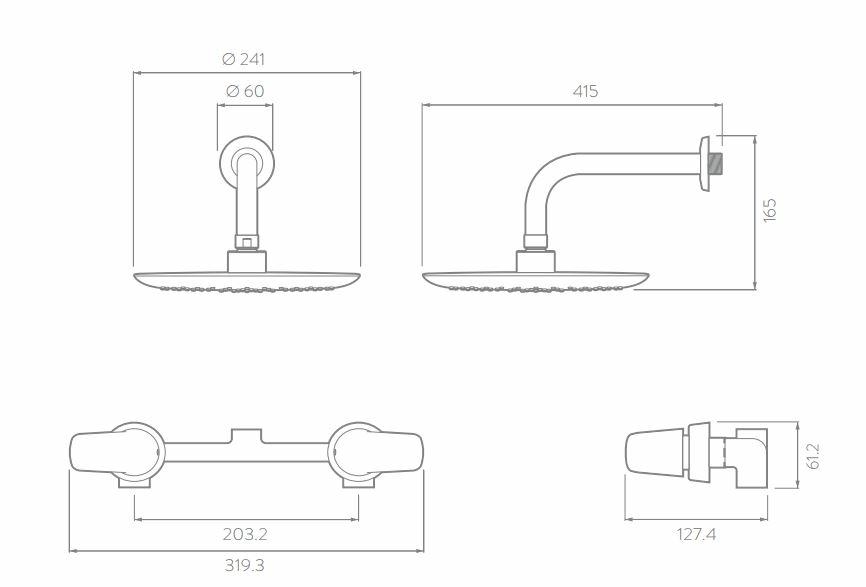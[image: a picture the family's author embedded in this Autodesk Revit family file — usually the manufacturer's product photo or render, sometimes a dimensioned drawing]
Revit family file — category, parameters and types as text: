
# Revit family: LQ4045551  LQ4055551_Ducha 8 pulgadas SD Liquid
name_source: partatom
category: Plumbing Fixtures
units: mm (PartAtom-declared; Revit-internal decimal feet)

## family parameters
Always vertical = Yes
Cut with Voids When Loaded = No
Host = Wall
OmniClass Number = 23.45.05.14.17
OmniClass Title = Showers
Part Type = Normal
Room Calculation Point = No
Round Connector Dimension = Use Diameter
Shared = No

## types (1)
- Type 1
    Alto = 876 mm
    Altura ducha = 2000 mm  [stored 6.56168 ft]
    Altura mezclador = 1200 mm
    Ancho = 320 mm
    Capacidad de flujo = 80 psi: 8,6 L/min
    Fabricante = Corona
    Garantía = 30 años
    Material = Corona_Plastico_Cromado
    Peso Bruto aprox = 2.400 g. - 5,29 lb
    Peso neto = 2.130 g. - 4,70 lb
    Presion maxima = 125 psi (860 Kpa)
    Presion minima = 20 psi (140 Kpa)
    Profundidad = 395 mm
    Referencia = LQ4045551 / LQ4055551
    Temperaturas máxima de trabajo = 71˚C / 159,8˚F
    Temperaturas mínima de trabajo = 5˚C / 41 ˚F
    URL_Mezclador = https://corona.co
    URL_Regadera = https://corona.co

note: [stored X ft] marks values corroborated as IEEE doubles in the binary element streams (Revit-internal decimal feet)

## geometry (parser evidence)
native form markers: Sweep x13
no freeform markers — native parametric forms only
